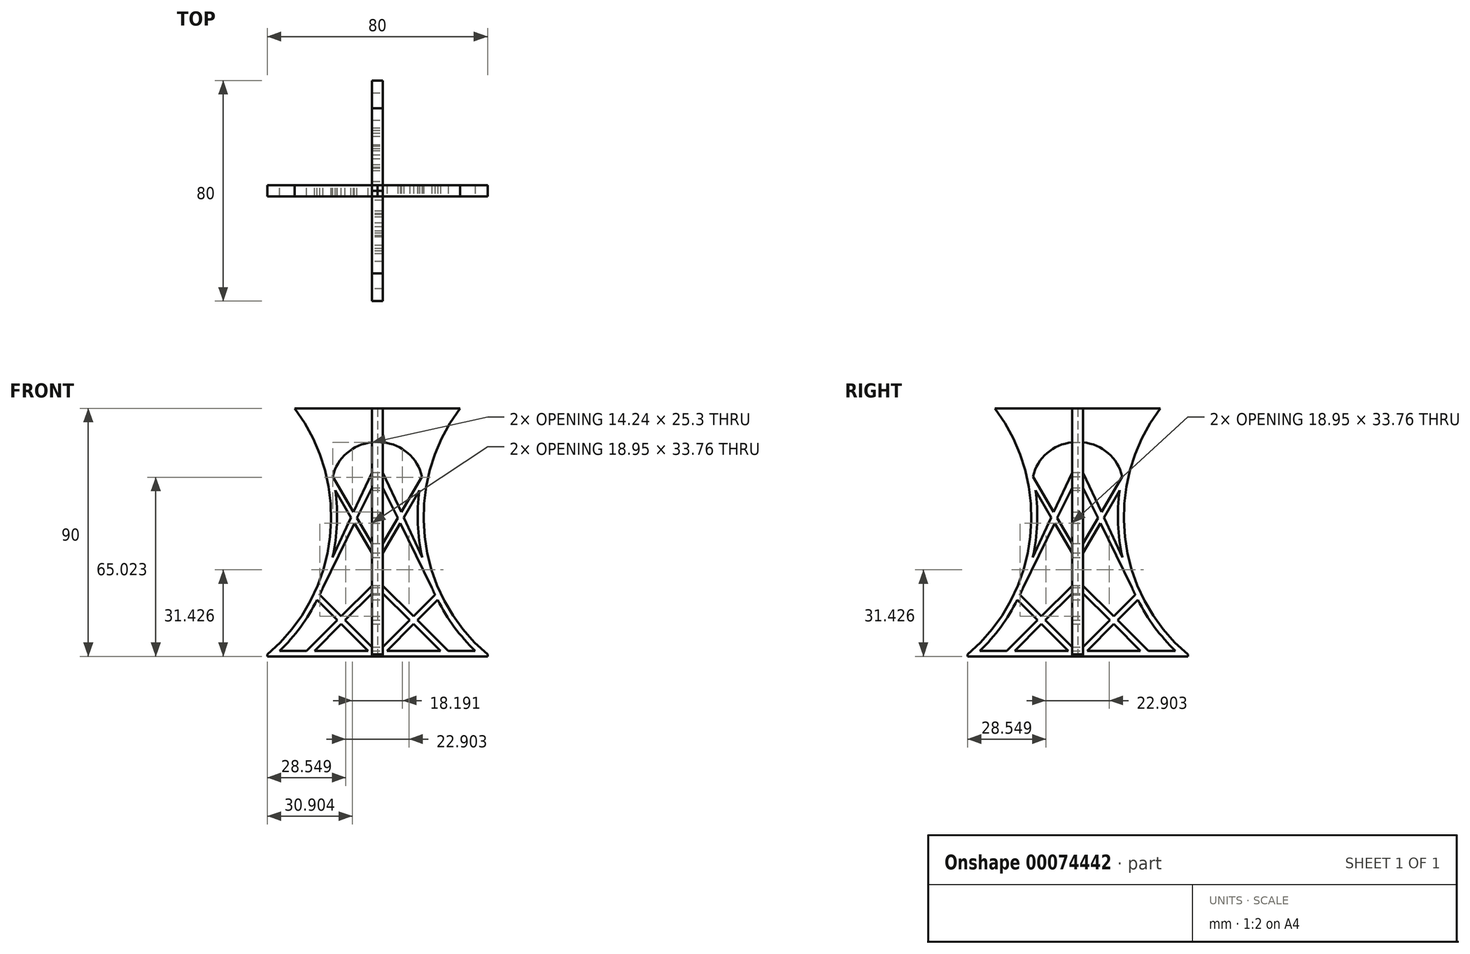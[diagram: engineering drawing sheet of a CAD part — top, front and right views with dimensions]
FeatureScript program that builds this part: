
annotation { "Feature Type Name" : "Feature", "Feature Type Description" : "" }
export const myFeature = defineFeature(function(context is Context, id is Id, definition is map)
    precondition{}
    {
        {
            var Q0;
            Q0=qCreatedBy(makeId("Right.planeOp"),FACE);
            var sketch = newSketch(context, id + "F0", { "sketchPlane" : qUnion([Q0])});
            skLineSegment(sketch, "E0", {"start": v(-30, 90) * mm, "end": v(0, 90) * mm});
            skLineSegment(sketch, "E1", {"start": v(0, 90) * mm, "end": v(0, 0) * mm});
            skLineSegment(sketch, "E2", {"start": v(0, 0) * mm, "end": v(-40, 0) * mm});
            skLineSegment(sketch, "E3", {"start": v(-40, 0) * mm, "end": v(-40, 0.68) * mm});
            skArc(sketch, "E4", {"start": v(-40, 0.68) * mm, "mid": v(-17.2, 43.35) * mm, "end": v(-30, 90) * mm});
            skArc(sketch, "E5.0", {"start": v(-35.54, 2) * mm, "mid": v(-27.93, 10.66) * mm, "end": v(-21.9, 20.5) * mm});
            skLineSegment(sketch, "E6", {"start": v(-25.69, 2) * mm, "end": v(-14.55, 13.13) * mm});
            skLineSegment(sketch, "E7", {"start": v(-22.86, 2) * mm, "end": v(-13.14, 11.72) * mm});
            skLineSegment(sketch, "E8", {"start": v(-1.97, 3.38) * mm, "end": v(-11.72, 13.13) * mm});
            skLineSegment(sketch, "E9", {"start": v(-3.42, 2) * mm, "end": v(-13.14, 11.72) * mm});
            skPoint(sketch, "E10.center", {"position": v(-13.14, 13.13) * mm});
            skPoint(sketch, "E11.startSnap0", {"position": v(-14.16, 4.05) * mm});
            skLineSegment(sketch, "E12.trimOffspring", {"start": v(-3.42, 2) * mm, "end": v(-35.54, 2) * mm});
            skLineSegment(sketch, "E13", {"start": v(-1.97, 77.68) * mm, "end": v(-1.97, 40.98) * mm});
            skArc(sketch, "E14.trimOffspring", {"start": v(-35.54, 2) * mm, "mid": v(-27.9, 10.63) * mm, "end": v(-21.85, 20.44) * mm});
            skLineSegment(sketch, "E15", {"start": v(-16.29, 35.94) * mm, "end": v(-9.55, 50.43) * mm});
            skLineSegment(sketch, "E16", {"start": v(-1.97, 61.2) * mm, "end": v(-7.38, 50.2) * mm});
            skLineSegment(sketch, "E17", {"start": v(-16.22, 65.3) * mm, "end": v(-8.65, 52.37) * mm});
            skLineSegment(sketch, "E18", {"start": v(-1.97, 37.5) * mm, "end": v(-8.3, 48.3) * mm});
            skLineSegment(sketch, "E19.trimOffspring", {"start": v(-8.65, 52.37) * mm, "end": v(-1.97, 66.72) * mm});
            skLineSegment(sketch, "E20.trimOffspring", {"start": v(-9.55, 50.43) * mm, "end": v(-15.3, 60.26) * mm});
            skLineSegment(sketch, "E21.trimOffspring", {"start": v(-7.38, 50.2) * mm, "end": v(-1.97, 40.98) * mm});
            skLineSegment(sketch, "E22.trimOffspring", {"start": v(-1.97, 37.5) * mm, "end": v(-1.97, 3.38) * mm});
            skArc(sketch, "E23.trimOffspring", {"start": v(-16.29, 35.94) * mm, "mid": v(-14.7, 48.05) * mm, "end": v(-15.3, 60.26) * mm});
            skLineSegment(sketch, "E24.trimOffspring", {"start": v(-8.3, 48.3) * mm, "end": v(-19.79, 24.93) * mm});
            skArc(sketch, "E25", {"start": v(-1.97, 77.68) * mm, "mid": v(-11.09, 73.78) * mm, "end": v(-16.22, 65.3) * mm});
            skArc(sketch, "E26.trimOffspring", {"start": v(-20.93, 22.35) * mm, "mid": v(-20.35, 23.63) * mm, "end": v(-19.79, 24.93) * mm});
            skLineSegment(sketch, "E27.trimOffspring", {"start": v(-13.13, 14.55) * mm, "end": v(-1.97, 25.7) * mm});
            skLineSegment(sketch, "E28.trimOffspring", {"start": v(-14.55, 13.13) * mm, "end": v(-21.9, 20.5) * mm});
            skLineSegment(sketch, "E29.trimOffspring", {"start": v(-11.72, 13.13) * mm, "end": v(-1.97, 22.87) * mm});
            skLineSegment(sketch, "E30.trimOffspring", {"start": v(-13.13, 14.55) * mm, "end": v(-20.93, 22.35) * mm});
            skSolve(sketch);
        }
        {
            var Q0;
            Q0=qSketchRegion(id+"F0",true);
            extrude(context, id + "F1", {"entities" : qUnion([Q0]), "depth" : 2 * mm, "hasSecondDirection" : true, "secondDirectionOppositeDirection" : true, "secondDirectionDepth" : 2 * mm});
        }
        {
            var Q0;
            Q0=qCreatedBy(makeId("Right.planeOp"),FACE);
            var sketch = newSketch(context, id + "F2", { "sketchPlane" : qUnion([Q0])});
            skLineSegment(sketch, "E31", {"start": v(0, 81) * mm, "end": v(0, -28.5) * mm, "construction": true});
            skSolve(sketch);
        }
        {
            var Q0;
            Q0=makeQuery(id+"F1.opExtrude","SWEPT_BODY",BODY,{"disambiguationData":[OSD([sQuery(id+"F0.wireOp",EDGE,"E0"),sQuery(id+"F0.wireOp",EDGE,"E1"),sQuery(id+"F0.wireOp",EDGE,"N8EfN9Iy-VFxy-i62X-S3Tn-et34u0hB6ofw"),sQuery(id+"F0.wireOp",EDGE,"ofOerVMI-8AtS-AqWo-Xm8z-ZVAlB3EUovam"),sQuery(id+"F0.wireOp",EDGE,"ba3e6201-bb00-4176-be12-0bcf97df4df2"),sQuery(id+"F0.wireOp",EDGE,"k6Ju8hmT-RXya-gFIe-6RDm-fDKX84Fwp2G4"),sQuery(id+"F0.wireOp",EDGE,"dTDJtstR-zKxY-rc8w-sIGn-4ASnDpw26A23"),sQuery(id+"F0.wireOp",EDGE,"Cvr0LfUC-tO0D-IxcI-B5Ti-WW2sAGeSHFF8"),sQuery(id+"F0.wireOp",EDGE,"DwRJblST-1CEV-pcTT-NFQT-YytcCcE5cTGx"),sQuery(id+"F0.wireOp",EDGE,"973229ff-babc-457a-ac66-6eeaf75bea45")])]});
            var Q1;
            Q1=sQuery(id+"F2.wireOp",EDGE,"E31");
            circularPattern(context, id + "F3", {"entities" : qUnion([Q0]), "axis" : qUnion([Q1]), "angle" : 90 * degree, "instanceCount" : round(4)});
        }
    });
